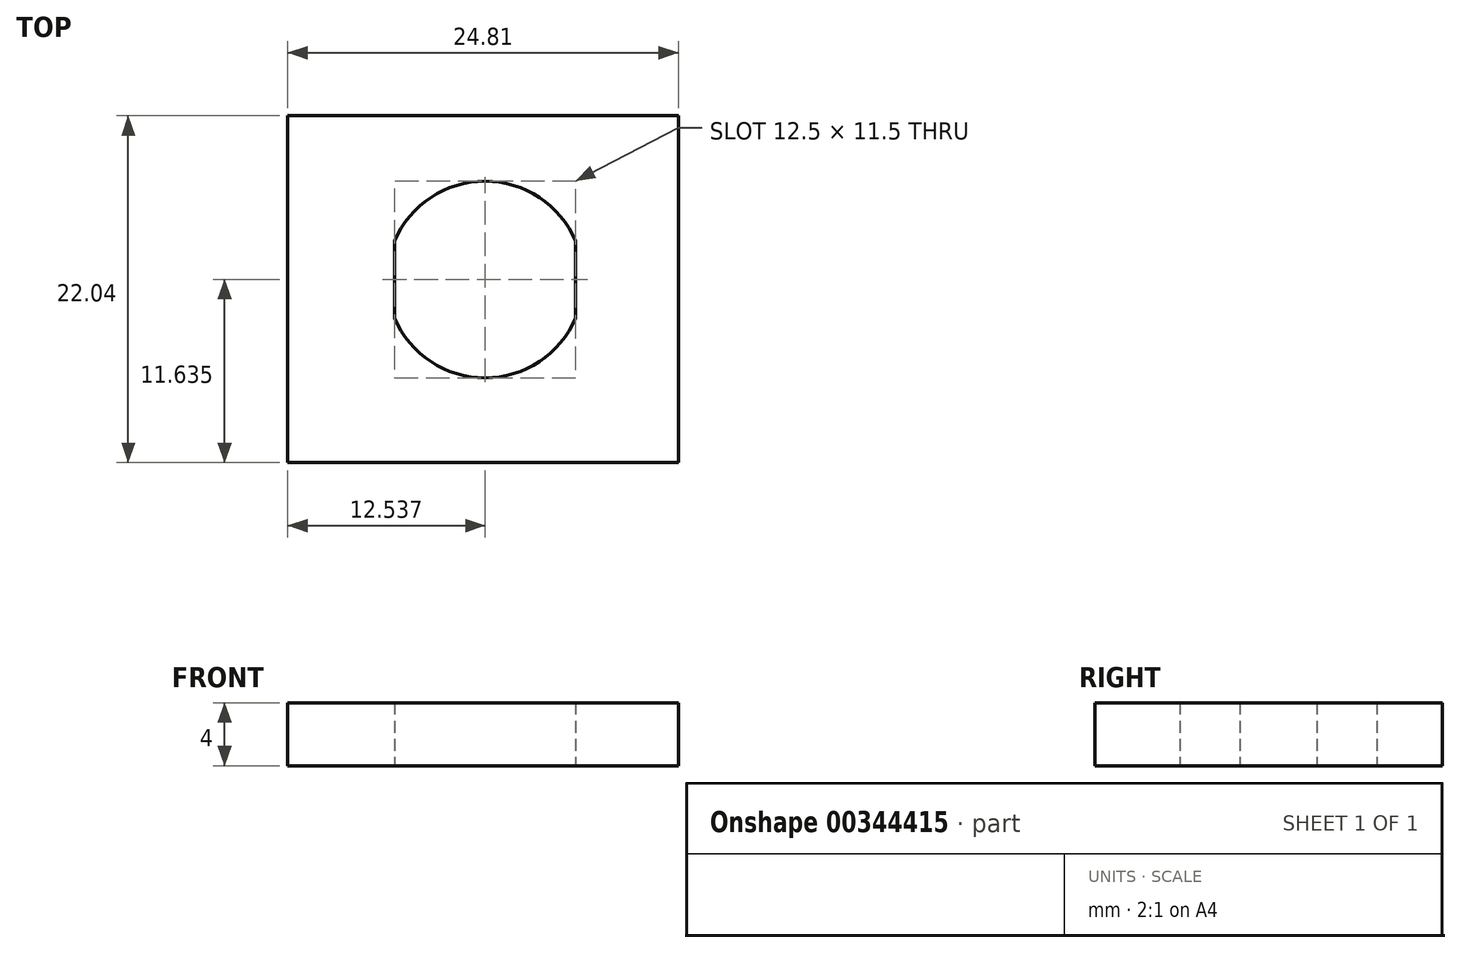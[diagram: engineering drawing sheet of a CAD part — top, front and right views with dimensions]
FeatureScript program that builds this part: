
annotation { "Feature Type Name" : "Feature", "Feature Type Description" : "" }
export const myFeature = defineFeature(function(context is Context, id is Id, definition is map)
    precondition{}
    {
        {
            var Q0;
            Q0=qCreatedBy(makeId("Top.planeOp"),FACE);
            var sketch = newSketch(context, id + "F0", { "sketchPlane" : qUnion([Q0])});
            skLineSegment(sketch, "E0", {"start": v(-26.65, 7.62) * mm, "end": v(-26.65, 12.51) * mm});
            skLineSegment(sketch, "E1", {"start": v(-15.15, 7.62) * mm, "end": v(-15.15, 12.51) * mm});
            skLineSegment(sketch, "E2", {"start": v(-26.65, 10.06) * mm, "end": v(-15.15, 10.06) * mm, "construction": true});
            skArc(sketch, "E3", {"start": v(-26.65, 12.51) * mm, "mid": v(-20.9, 16.31) * mm, "end": v(-15.15, 12.51) * mm});
            skArc(sketch, "E4", {"start": v(-26.65, 7.62) * mm, "mid": v(-20.9, 3.81) * mm, "end": v(-15.15, 7.62) * mm});
            skLineSegment(sketch, "E5.bottom", {"start": v(-33.44, 20.47) * mm, "end": v(-8.63, 20.47) * mm});
            skLineSegment(sketch, "E5.top", {"start": v(-33.44, -1.57) * mm, "end": v(-8.63, -1.57) * mm});
            skLineSegment(sketch, "E5.left", {"start": v(-33.44, 20.47) * mm, "end": v(-33.44, -1.57) * mm});
            skLineSegment(sketch, "E5.right", {"start": v(-8.63, 20.47) * mm, "end": v(-8.63, -1.57) * mm});
            skSolve(sketch);
        }
        {
            var Q0;
            Q0 = qSketchRegion(id + "F0", true);
            extrude(context, id + "F1", {"entities" : qUnion([Q0]), "depth" : 4 * mm});
        }
    });
